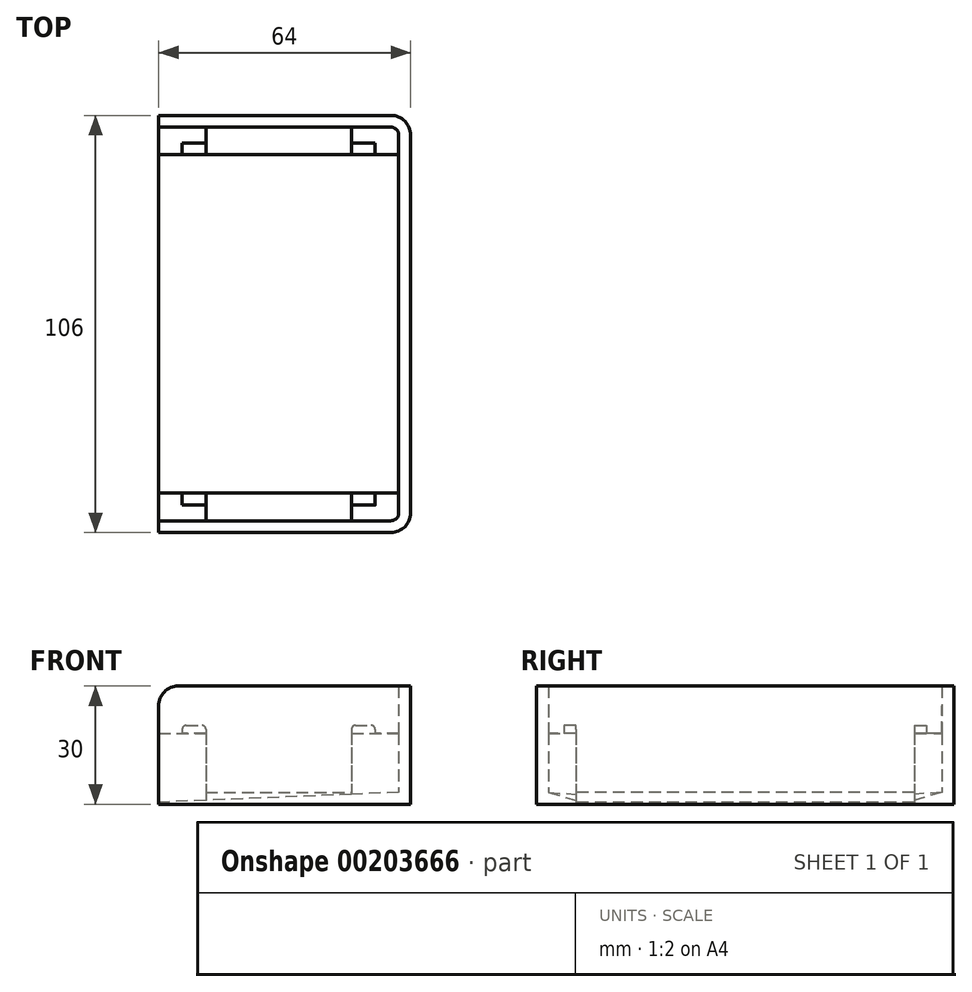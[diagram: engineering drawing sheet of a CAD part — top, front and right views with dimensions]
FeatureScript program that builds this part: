
annotation { "Feature Type Name" : "Feature", "Feature Type Description" : "" }
export const myFeature = defineFeature(function(context is Context, id is Id, definition is map)
    precondition{}
    {
        {
            var Q0;
            Q0=qCreatedBy(makeId("Top.planeOp"),FACE);
            var sketch = newSketch(context, id + "F0", { "sketchPlane" : qUnion([Q0])});
            skLineSegment(sketch, "E0.bottom", {"start": v(29, -50) * mm, "end": v(-29, -50) * mm});
            skLineSegment(sketch, "E0.top", {"start": v(29, 50) * mm, "end": v(-29, 50) * mm});
            skLineSegment(sketch, "E0.left", {"start": v(29, -50) * mm, "end": v(29, 50) * mm});
            skLineSegment(sketch, "E0.right", {"start": v(-29, -50) * mm, "end": v(-29, 50) * mm});
            skPoint(sketch, "E0.middle", {"position": v(0, 0) * mm});
            skLineSegment(sketch, "E1.bottom", {"start": v(32, -53) * mm, "end": v(-32, -53) * mm});
            skLineSegment(sketch, "E1.top", {"start": v(32, 53) * mm, "end": v(-32, 53) * mm});
            skLineSegment(sketch, "E1.left", {"start": v(32, -53) * mm, "end": v(32, 53) * mm});
            skLineSegment(sketch, "E1.right", {"start": v(-32, -53) * mm, "end": v(-32, 53) * mm});
            skSolve(sketch);
        }
        {
            var Q0;
            Q0=makeQuery(id+"F0.imprint","IMPRINT",FACE,{"disambiguationData":[TD([[makeQuery(id+"F0.imprint","IMPRINT",EDGE,{"derivedFrom":sQuery(id+"F0.wireOp",EDGE,"E0.bottom")}),1.0]])]});
            var Q1;
            Q1=makeQuery(id+"F0.imprint","IMPRINT",FACE,{"disambiguationData":[TD([[makeQuery(id+"F0.imprint","IMPRINT",EDGE,{"derivedFrom":sQuery(id+"F0.wireOp",EDGE,"E0.bottom")}),-1.0]])]});
            extrude(context, id + "F1", {"entities" : qUnion([Q0, Q1]), "depth" : 3 * mm});
        }
        {
            var Q0;
            Q0 = qSketchRegion(id + "F0", true);
            extrude(context, id + "F2", {"entities" : qUnion([Q0]), "operationType" : NewBodyOperationType.ADD, "depth" : 30 * mm});
        }
        {
            var Q0;
            {var subQ0=sQuery(id+"F0.wireOp",EDGE,"E1.right");Q0=makeQuery(id+"F2.boolean.opBoolean","MERGE",FACE,{"derivedFrom":[makeQuery(id+"F1.opExtrude","SWEPT_FACE",FACE,{"disambiguationData":[OSD([subQ0])]}),makeQuery(id+"F2.opExtrude","SWEPT_FACE",FACE,{"disambiguationData":[OSD([subQ0])]})]});}
            var sketch = newSketch(context, id + "F3", { "sketchPlane" : qUnion([Q0])});
            skLineSegment(sketch, "E2.0", {"start": v(-50, 30) * mm, "end": v(-50, 3) * mm});
            skLineSegment(sketch, "E2.1", {"start": v(50, 30) * mm, "end": v(50, 3) * mm});
            skLineSegment(sketch, "E3.0", {"start": v(-50, 3) * mm, "end": v(50, 3) * mm});
            skLineSegment(sketch, "E4", {"start": v(-50, 30) * mm, "end": v(-50, 36.14) * mm});
            skLineSegment(sketch, "E5", {"start": v(-50, 36.14) * mm, "end": v(50, 36.14) * mm});
            skLineSegment(sketch, "E6", {"start": v(50, 36.14) * mm, "end": v(50, 30) * mm});
            skSolve(sketch);
        }
        {
            var Q0;
            Q0 = qSketchRegion(id + "F3", true);
            extrude(context, id + "F4", {"entities" : qUnion([Q0]), "operationType" : NewBodyOperationType.REMOVE, "endBound" : BoundingType.UP_TO_NEXT, "oppositeDirection" : true, "depth" : 25 * mm});
        }
        {
            var Q0;
            Q0=makeQuery(id+"F4.boolean.opBoolean","MERGE",FACE,{"derivedFrom":[makeQuery(id+"F1.opExtrude","CAP_FACE",FACE,{"disambiguationData":[OSD([sQuery(id+"F0.wireOp",EDGE,"E1.bottom"),sQuery(id+"F0.wireOp",EDGE,"E1.top"),sQuery(id+"F0.wireOp",EDGE,"E1.left"),sQuery(id+"F0.wireOp",EDGE,"E1.right")])],"isStart":false}),makeQuery(id+"F4.opExtrude","SWEPT_FACE",FACE,{"disambiguationData":[OSD([sQuery(id+"F3.wireOp",EDGE,"E3.0")])]})]});
            var sketch = newSketch(context, id + "F5", { "sketchPlane" : qUnion([Q0])});
            skLineSegment(sketch, "E7.0", {"start": v(29, 50) * mm, "end": v(-32, 50) * mm, "construction": true});
            skLineSegment(sketch, "E7.1", {"start": v(29, -50) * mm, "end": v(29, 50) * mm, "construction": true});
            skLineSegment(sketch, "E7.2", {"start": v(29, -50) * mm, "end": v(-32, -50) * mm, "construction": true});
            skLineSegment(sketch, "E8.bottom", {"start": v(-32, 50) * mm, "end": v(-20, 50) * mm});
            skLineSegment(sketch, "E8.top", {"start": v(-32, 43) * mm, "end": v(-20, 43) * mm});
            skLineSegment(sketch, "E8.left", {"start": v(-32, 50) * mm, "end": v(-32, 43) * mm});
            skLineSegment(sketch, "E8.right", {"start": v(-20, 50) * mm, "end": v(-20, 43) * mm});
            skLineSegment(sketch, "E9.bottom", {"start": v(29, 50) * mm, "end": v(17, 50) * mm});
            skLineSegment(sketch, "E9.top", {"start": v(29, 43) * mm, "end": v(17, 43) * mm});
            skLineSegment(sketch, "E9.left", {"start": v(29, 50) * mm, "end": v(29, 43) * mm});
            skLineSegment(sketch, "E9.right", {"start": v(17, 50) * mm, "end": v(17, 43) * mm});
            skLineSegment(sketch, "E10.bottom", {"start": v(29, -50) * mm, "end": v(17, -50) * mm});
            skLineSegment(sketch, "E10.top", {"start": v(29, -43) * mm, "end": v(17, -43) * mm});
            skLineSegment(sketch, "E10.left", {"start": v(29, -50) * mm, "end": v(29, -43) * mm});
            skLineSegment(sketch, "E10.right", {"start": v(17, -50) * mm, "end": v(17, -43) * mm});
            skLineSegment(sketch, "E11.bottom", {"start": v(-32, -50) * mm, "end": v(-20, -50) * mm});
            skLineSegment(sketch, "E11.top", {"start": v(-32, -43) * mm, "end": v(-20, -43) * mm});
            skLineSegment(sketch, "E11.left", {"start": v(-32, -50) * mm, "end": v(-32, -43) * mm});
            skLineSegment(sketch, "E11.right", {"start": v(-20, -50) * mm, "end": v(-20, -43) * mm});
            skSolve(sketch);
        }
        {
            var Q0;
            Q0 = qSketchRegion(id + "F5", true);
            extrude(context, id + "F6", {"entities" : qUnion([Q0]), "operationType" : NewBodyOperationType.ADD, "depth" : 15 * mm});
        }
        {
            var Q0;
            Q0=makeQuery(id+"F6.opExtrude","CAP_FACE",FACE,{"disambiguationData":[OSD([sQuery(id+"F5.wireOp",EDGE,"E8.bottom"),sQuery(id+"F5.wireOp",EDGE,"E8.top"),sQuery(id+"F5.wireOp",EDGE,"E8.left"),sQuery(id+"F5.wireOp",EDGE,"E8.right")])],"isStart":false});
            var sketch = newSketch(context, id + "F7", { "sketchPlane" : qUnion([Q0])});
            skPoint(sketch, "E12.0", {"position": v(-20, -43) * mm});
            skPoint(sketch, "E12.1", {"position": v(17, -43) * mm});
            skPoint(sketch, "E12.2", {"position": v(17, 43) * mm});
            skLineSegment(sketch, "E13.bottom", {"start": v(17, 43) * mm, "end": v(23, 43) * mm});
            skLineSegment(sketch, "E13.top", {"start": v(17, 46) * mm, "end": v(23, 46) * mm});
            skLineSegment(sketch, "E13.left", {"start": v(17, 43) * mm, "end": v(17, 46) * mm});
            skLineSegment(sketch, "E13.right", {"start": v(23, 43) * mm, "end": v(23, 46) * mm});
            skLineSegment(sketch, "E14.bottom", {"start": v(17, -43) * mm, "end": v(23, -43) * mm});
            skLineSegment(sketch, "E14.top", {"start": v(17, -46) * mm, "end": v(23, -46) * mm});
            skLineSegment(sketch, "E14.left", {"start": v(17, -43) * mm, "end": v(17, -46) * mm});
            skLineSegment(sketch, "E14.right", {"start": v(23, -43) * mm, "end": v(23, -46) * mm});
            skLineSegment(sketch, "E15.bottom", {"start": v(-20, -43) * mm, "end": v(-26, -43) * mm});
            skLineSegment(sketch, "E15.top", {"start": v(-20, -46) * mm, "end": v(-26, -46) * mm});
            skLineSegment(sketch, "E15.left", {"start": v(-20, -43) * mm, "end": v(-20, -46) * mm});
            skLineSegment(sketch, "E15.right", {"start": v(-26, -43) * mm, "end": v(-26, -46) * mm});
            skLineSegment(sketch, "E16.bottom", {"start": v(-20, 43) * mm, "end": v(-26, 43) * mm});
            skLineSegment(sketch, "E16.top", {"start": v(-20, 46) * mm, "end": v(-26, 46) * mm});
            skLineSegment(sketch, "E16.left", {"start": v(-20, 43) * mm, "end": v(-20, 46) * mm});
            skLineSegment(sketch, "E16.right", {"start": v(-26, 43) * mm, "end": v(-26, 46) * mm});
            skSolve(sketch);
        }
        {
            var Q0;
            Q0 = qSketchRegion(id + "F7", true);
            extrude(context, id + "F8", {"entities" : qUnion([Q0]), "operationType" : NewBodyOperationType.ADD, "depth" : 2 * mm});
        }
        {
            var Q0;
            Q0=qCreatedBy(makeId("Front.planeOp"),FACE);
            var sketch = newSketch(context, id + "F9", { "sketchPlane" : qUnion([Q0])});
            skLineSegment(sketch, "E17.0.0", {"start": v(-32, 0) * mm, "end": v(32, 0) * mm, "construction": true});
            skLineSegment(sketch, "E17.0.1", {"start": v(32, 0) * mm, "end": v(32, 30) * mm, "construction": true});
            skLineSegment(sketch, "E17.0.2", {"start": v(32, 30) * mm, "end": v(-32, 30) * mm, "construction": true});
            skLineSegment(sketch, "E17.0.3", {"start": v(-32, 30) * mm, "end": v(-32, 0) * mm, "construction": true});
            skLineSegment(sketch, "E18", {"start": v(-32, 0.5) * mm, "end": v(32, 3.12) * mm});
            skLineSegment(sketch, "E19", {"start": v(32, 3.12) * mm, "end": v(32, 0) * mm});
            skLineSegment(sketch, "E20", {"start": v(32, 0) * mm, "end": v(-32, 0) * mm});
            skLineSegment(sketch, "E21", {"start": v(-32, 0.5) * mm, "end": v(-32, 0) * mm});
            skLineSegment(sketch, "E22", {"start": v(-32, 0.5) * mm, "end": v(32, 0.5) * mm, "construction": true});
            skLineSegment(sketch, "E23", {"start": v(-32, 0.5) * mm, "end": v(-32, 30) * mm});
            skLineSegment(sketch, "E24", {"start": v(32, 30) * mm, "end": v(-32, 30) * mm});
            skLineSegment(sketch, "E25", {"start": v(32, 3.12) * mm, "end": v(32, 30) * mm});
            skLineSegment(sketch, "E26.0", {"start": v(29, 30) * mm, "end": v(29, 18) * mm});
            skLineSegment(sketch, "E27", {"start": v(29, 18) * mm, "end": v(29, 3) * mm});
            skSolve(sketch);
        }
        {
            var Q0;
            {var subQ1=sQuery(id+"F9.wireOp",EDGE,"E23");Q0=makeQuery(id+"F9.imprint","IMPRINT",FACE,{"disambiguationData":[TD([[makeQuery(id+"F9.imprint","IMPRINT",EDGE,{"derivedFrom":subQ1}),-1.0]])]});}
            var Q1;
            Q1=makeQuery(id+"F8.boolean.opBoolean","MERGE",FACE,{"derivedFrom":[makeQuery(id+"F6.opExtrude","SWEPT_FACE",FACE,{"disambiguationData":[OSD([sQuery(id+"F5.wireOp",EDGE,"E9.top")])]}),makeQuery(id+"F8.opExtrude","SWEPT_FACE",FACE,{"disambiguationData":[OSD([sQuery(id+"F7.wireOp",EDGE,"E13.bottom")])]})]});
            var Q2;
            Q2=makeQuery(id+"F8.boolean.opBoolean","MERGE",FACE,{"derivedFrom":[makeQuery(id+"F6.opExtrude","SWEPT_FACE",FACE,{"disambiguationData":[OSD([sQuery(id+"F5.wireOp",EDGE,"E10.top")])]}),makeQuery(id+"F8.opExtrude","SWEPT_FACE",FACE,{"disambiguationData":[OSD([sQuery(id+"F7.wireOp",EDGE,"E14.bottom")])]})]});
            extrude(context, id + "F10", {"entities" : qUnion([Q0]), "operationType" : NewBodyOperationType.REMOVE, "endBound" : BoundingType.UP_TO_SURFACE, "oppositeDirection" : true, "endBoundEntityFace" : qUnion([Q1]), "depth" : 25 * mm, "hasSecondDirection" : true, "secondDirectionBound" : SecondDirectionBoundingType.UP_TO_SURFACE, "secondDirectionOppositeDirection" : false, "secondDirectionBoundEntityFace" : qUnion([Q2]), "secondDirectionDepth" : 25 * mm});
        }
        {
            var Q0;
            Q0=makeQuery(id+"F8.boolean.opBoolean","MERGE",FACE,{"derivedFrom":[makeQuery(id+"F6.opExtrude","SWEPT_FACE",FACE,{"disambiguationData":[OSD([sQuery(id+"F5.wireOp",EDGE,"E10.right")])]}),makeQuery(id+"F8.opExtrude","SWEPT_FACE",FACE,{"disambiguationData":[OSD([sQuery(id+"F7.wireOp",EDGE,"E14.left")])]})]});
            var sketch = newSketch(context, id + "F11", { "sketchPlane" : qUnion([Q0])});
            skLineSegment(sketch, "E28.0", {"start": v(50, 3) * mm, "end": v(43, 3) * mm, "construction": true});
            skLineSegment(sketch, "E29.0", {"start": v(43, 3) * mm, "end": v(43, 0.5) * mm, "construction": true});
            skLineSegment(sketch, "E30", {"start": v(50, 3) * mm, "end": v(43, 2.5) * mm});
            skLineSegment(sketch, "E31", {"start": v(0, 0) * mm, "end": v(0, 54.01) * mm, "construction": true});
            skLineSegment(sketch, "E32", {"start": v(43, 2.5) * mm, "end": v(43, 3) * mm});
            skLineSegment(sketch, "E33", {"start": v(43, 3) * mm, "end": v(50, 3) * mm});
            skLineSegment(sketch, "E34.MirrorCS", {"start": v(-43, 2.5) * mm, "end": v(-43, 3) * mm});
            skLineSegment(sketch, "E35.MirrorCS", {"start": v(-43, 3) * mm, "end": v(-50, 3) * mm});
            skLineSegment(sketch, "E36.MirrorCS", {"start": v(-50, 3) * mm, "end": v(-43, 2.5) * mm});
            skLineSegment(sketch, "E37.MirrorCS", {"start": v(-43, 3) * mm, "end": v(-43, 0.5) * mm, "construction": true});
            skLineSegment(sketch, "E38.MirrorCS", {"start": v(-50, 3) * mm, "end": v(-43, 3) * mm, "construction": true});
            skSolve(sketch);
        }
        {
            var Q0;
            Q0=makeQuery(id+"F8.boolean.opBoolean","MERGE",FACE,{"derivedFrom":[makeQuery(id+"F6.opExtrude","SWEPT_FACE",FACE,{"disambiguationData":[OSD([sQuery(id+"F5.wireOp",EDGE,"E11.right")])]}),makeQuery(id+"F8.opExtrude","SWEPT_FACE",FACE,{"disambiguationData":[OSD([sQuery(id+"F7.wireOp",EDGE,"E15.left")])]})]});
            var sketch = newSketch(context, id + "F12", { "sketchPlane" : qUnion([Q0])});
            skLineSegment(sketch, "E39.0", {"start": v(-50, 3) * mm, "end": v(-43, 3) * mm, "construction": true});
            skLineSegment(sketch, "E40.0", {"start": v(-43, 3) * mm, "end": v(-43, 0.5) * mm, "construction": true});
            skLineSegment(sketch, "E41", {"start": v(-50, 3) * mm, "end": v(-43, 1) * mm});
            skLineSegment(sketch, "E42", {"start": v(-43, 1) * mm, "end": v(-43, 3) * mm});
            skLineSegment(sketch, "E43", {"start": v(-50, 3) * mm, "end": v(-43, 3) * mm});
            skLineSegment(sketch, "E44", {"start": v(0, -0.53) * mm, "end": v(0, 9.82) * mm, "construction": true});
            skLineSegment(sketch, "E45.MirrorCS", {"start": v(50, 3) * mm, "end": v(43, 3) * mm});
            skLineSegment(sketch, "E46.MirrorCS", {"start": v(43, 1) * mm, "end": v(43, 3) * mm});
            skLineSegment(sketch, "E47.MirrorCS", {"start": v(50, 3) * mm, "end": v(43, 1) * mm});
            skLineSegment(sketch, "E48.MirrorCS", {"start": v(43, 3) * mm, "end": v(43, 0.5) * mm, "construction": true});
            skLineSegment(sketch, "E49.MirrorCS", {"start": v(50, 3) * mm, "end": v(43, 3) * mm, "construction": true});
            skSolve(sketch);
        }
        {
            var Q1;
            Q1=makeQuery(id+"F11.imprint","IMPRINT",FACE,{"disambiguationData":[TD([[makeQuery(id+"F11.imprint","IMPRINT",EDGE,{"derivedFrom":sQuery(id+"F11.wireOp",EDGE,"E34.MirrorCS")}),1.0]])]});
            var Q2;
            Q2=makeQuery(id+"F12.imprint","IMPRINT",FACE,{"disambiguationData":[TD([[makeQuery(id+"F12.imprint","IMPRINT",EDGE,{"derivedFrom":sQuery(id+"F12.wireOp",EDGE,"E45.MirrorCS")}),1.0]])]});
            loft(context, id + "F13", {"operationType" : NewBodyOperationType.REMOVE, "sheetProfilesArray" : [{ "sheetProfileEntities" : qUnion([Q1]) }, { "sheetProfileEntities" : qUnion([Q2]) }]});
        }
        {
            var Q1;
            Q1=makeQuery(id+"F11.imprint","IMPRINT",FACE,{"disambiguationData":[TD([[makeQuery(id+"F11.imprint","IMPRINT",EDGE,{"derivedFrom":sQuery(id+"F11.wireOp",EDGE,"E30")}),-1.0]])]});
            var Q2;
            Q2=makeQuery(id+"F12.imprint","IMPRINT",FACE,{"disambiguationData":[TD([[makeQuery(id+"F12.imprint","IMPRINT",EDGE,{"derivedFrom":sQuery(id+"F12.wireOp",EDGE,"E41")}),1.0]])]});
            loft(context, id + "F14", {"operationType" : NewBodyOperationType.REMOVE, "sheetProfilesArray" : [{ "sheetProfileEntities" : qUnion([Q1]) }, { "sheetProfileEntities" : qUnion([Q2]) }]});
        }
        {
            var Q0;
            Q0=makeQuery(id+"F8.opExtrude","CAP_EDGE",EDGE,{"disambiguationData":[OSD([sQuery(id+"F7.wireOp",EDGE,"E16.right")])],"isStart":false});
            var Q1;
            Q1=makeQuery(id+"F8.opExtrude","CAP_EDGE",EDGE,{"disambiguationData":[OSD([sQuery(id+"F7.wireOp",EDGE,"E16.left")])],"isStart":false});
            var Q2;
            Q2=makeQuery(id+"F8.opExtrude","CAP_EDGE",EDGE,{"disambiguationData":[OSD([sQuery(id+"F7.wireOp",EDGE,"E13.left")])],"isStart":false});
            var Q3;
            Q3=makeQuery(id+"F8.opExtrude","CAP_EDGE",EDGE,{"disambiguationData":[OSD([sQuery(id+"F7.wireOp",EDGE,"E13.right")])],"isStart":false});
            var Q4;
            Q4=makeQuery(id+"F8.opExtrude","CAP_EDGE",EDGE,{"disambiguationData":[OSD([sQuery(id+"F7.wireOp",EDGE,"E15.left")])],"isStart":false});
            var Q5;
            Q5=makeQuery(id+"F8.opExtrude","CAP_EDGE",EDGE,{"disambiguationData":[OSD([sQuery(id+"F7.wireOp",EDGE,"E15.right")])],"isStart":false});
            var Q6;
            Q6=makeQuery(id+"F8.opExtrude","CAP_EDGE",EDGE,{"disambiguationData":[OSD([sQuery(id+"F7.wireOp",EDGE,"E14.left")])],"isStart":false});
            var Q7;
            Q7=makeQuery(id+"F8.opExtrude","CAP_EDGE",EDGE,{"disambiguationData":[OSD([sQuery(id+"F7.wireOp",EDGE,"E14.right")])],"isStart":false});
            fillet(context, id + "F15", {"entities" : qUnion([Q0, Q1, Q2, Q3, Q4, Q5, Q6, Q7]), "radius" : 1 * mm, "tangentPropagation" : true, "allowEdgeOverflow" : false});
        }
        {
            var Q0;
            {var subQ0=sQuery(id+"F0.wireOp",EDGE,"E1.right");var subQ1=sQuery(id+"F0.wireOp",EDGE,"E1.bottom");Q0=makeQuery(id+"F4.boolean.opBoolean","SPLIT",EDGE,{"disambiguationData":[TD([makeQuery(id+"F1.opExtrude","SWEPT_FACE",FACE,{"disambiguationData":[OSD([subQ1])]})])],"derivedFrom":makeQuery(id+"F2.opExtrude","CAP_EDGE",EDGE,{"disambiguationData":[OSD([subQ0])],"isStart":false})});}
            var Q1;
            {var subQ1=sQuery(id+"F0.wireOp",EDGE,"E1.right");var subQ2=sQuery(id+"F0.wireOp",EDGE,"E1.top");Q1=makeQuery(id+"F4.boolean.opBoolean","SPLIT",EDGE,{"disambiguationData":[TD([makeQuery(id+"F1.opExtrude","SWEPT_FACE",FACE,{"disambiguationData":[OSD([subQ2])]})])],"derivedFrom":makeQuery(id+"F2.opExtrude","CAP_EDGE",EDGE,{"disambiguationData":[OSD([subQ1])],"isStart":false})});}
            fillet(context, id + "F16", {"entities" : qUnion([Q0, Q1]), "radius" : 5 * mm, "tangentPropagation" : true, "allowEdgeOverflow" : false});
        }
        {
            var Q0;
            {var subQ0=sQuery(id+"F0.wireOp",EDGE,"E1.left");var subQ1=sQuery(id+"F0.wireOp",EDGE,"E1.top");Q0=makeQuery(id+"F2.boolean.opBoolean","MERGE",EDGE,{"derivedFrom":[makeQuery(id+"F1.opExtrude","SWEPT_EDGE",EDGE,{"disambiguationData":[OSD([subQ1,subQ0])]}),makeQuery(id+"F2.opExtrude","SWEPT_EDGE",EDGE,{"disambiguationData":[OSD([subQ1,subQ0])]})]});}
            var Q1;
            {var subQ0=sQuery(id+"F0.wireOp",EDGE,"E1.left");var subQ1=sQuery(id+"F0.wireOp",EDGE,"E1.bottom");Q1=makeQuery(id+"F2.boolean.opBoolean","MERGE",EDGE,{"derivedFrom":[makeQuery(id+"F1.opExtrude","SWEPT_EDGE",EDGE,{"disambiguationData":[OSD([subQ1,subQ0])]}),makeQuery(id+"F2.opExtrude","SWEPT_EDGE",EDGE,{"disambiguationData":[OSD([subQ1,subQ0])]})]});}
            fillet(context, id + "F17", {"entities" : qUnion([Q0, Q1]), "radius" : 5 * mm, "tangentPropagation" : true, "allowEdgeOverflow" : false});
        }
        {
            var Q0;
            Q0=makeQuery(id+"F2.opExtrude","SWEPT_EDGE",EDGE,{"disambiguationData":[OSD([sQuery(id+"F0.wireOp",EDGE,"E0.top"),sQuery(id+"F0.wireOp",EDGE,"E0.left")])]});
            var Q1;
            Q1=makeQuery(id+"F2.opExtrude","SWEPT_EDGE",EDGE,{"disambiguationData":[OSD([sQuery(id+"F0.wireOp",EDGE,"E0.bottom"),sQuery(id+"F0.wireOp",EDGE,"E0.left")])]});
            var Q2;
            Q2=makeQuery(id+"F10.boolean.opBoolean","MERGE",EDGE,{"derivedFrom":[makeQuery(id+"F6.opExtrude","SWEPT_EDGE",EDGE,{"disambiguationData":[OSD([sQuery(id+"F3.wireOp",EDGE,"E3.0"),sQuery(id+"F5.wireOp",EDGE,"E8.top"),sQuery(id+"F5.wireOp",EDGE,"E8.left")])]}),makeQuery(id+"F10.opExtrude","TWEAK_EDGE",EDGE,{"derivedFrom":[makeQuery(id+"F8.boolean.opBoolean","MERGE",FACE,{"derivedFrom":[makeQuery(id+"F6.opExtrude","SWEPT_FACE",FACE,{"disambiguationData":[OSD([sQuery(id+"F5.wireOp",EDGE,"E9.top")])]}),makeQuery(id+"F8.opExtrude","SWEPT_FACE",FACE,{"disambiguationData":[OSD([sQuery(id+"F7.wireOp",EDGE,"E13.bottom")])]})]}),makeQuery(id+"F9.imprint","IMPRINT",EDGE,{"derivedFrom":sQuery(id+"F9.wireOp",EDGE,"E23")})]})]});
            var Q3;
            Q3=makeQuery(id+"F10.boolean.opBoolean","MERGE",EDGE,{"derivedFrom":[makeQuery(id+"F6.opExtrude","SWEPT_EDGE",EDGE,{"disambiguationData":[OSD([sQuery(id+"F3.wireOp",EDGE,"E3.0"),sQuery(id+"F5.wireOp",EDGE,"E11.top"),sQuery(id+"F5.wireOp",EDGE,"E11.left")])]}),makeQuery(id+"F10.opExtrude","TWEAK_EDGE",EDGE,{"derivedFrom":[makeQuery(id+"F8.boolean.opBoolean","MERGE",FACE,{"derivedFrom":[makeQuery(id+"F6.opExtrude","SWEPT_FACE",FACE,{"disambiguationData":[OSD([sQuery(id+"F5.wireOp",EDGE,"E10.top")])]}),makeQuery(id+"F8.opExtrude","SWEPT_FACE",FACE,{"disambiguationData":[OSD([sQuery(id+"F7.wireOp",EDGE,"E14.bottom")])]})]}),makeQuery(id+"F9.imprint","IMPRINT",EDGE,{"derivedFrom":sQuery(id+"F9.wireOp",EDGE,"E23")})]})]});
            fillet(context, id + "F18", {"entities" : qUnion([Q0, Q1, Q2, Q3]), "radius" : 2 * mm, "tangentPropagation" : true, "allowEdgeOverflow" : false});
        }
    });
